# Revit family: Shower-Valves_and_Controls-KALLISTA-Rough_In-P29527
name_source: partatom
category: Plumbing Fixtures
units: mm (PartAtom-declared; Revit-internal decimal feet)

## family parameters
Cut with Voids When Loaded = No
Host = Face
Maintain Annotation Orientation = No
OmniClass Number = 23.27.31.00
OmniClass Title = Valves
Part Type = Normal
Room Calculation Point = No
Round Connector Dimension = Use Diameter
Shared = No

## types (1)
- NA-Stainless Steel
    ADA Compliant = No
    Assembly Code = D2020
    CW Connection = Yes
    Cold Water Inlet = Cold Water Inlet
    Date Modified = 06/23/2025
    Default Elevation = 36"
    Description = 1/2 Inch Volume Control Rough-In Assembly
    Finish = Kallista-Metal-NA-Stainless_Steel
    Flow Rate = 0 GPM
    HW Connection = Yes
    Height = 2 3/8"
    Hot Water Inlet = Hot Water Inlet
    Length = 3 5/16"
    Manufacturer = Kallista Co.
    Master Format 2014 = 23 09 13.33
    Master Format 2014 Name = Control Valves
    Material = Premium Metal Construction
    Model = P29527-00-NA
    Pressure = 0.00 psi
    Product Documentation Link = https://techcomm.kohler.com
    Product Name = Rough In
    Product Page URL = https://www.kallista.com
    Type = 1
    URL = https://www.kallista.com
    Vent Connection = No
    Waste Connection = No
    Waste Water Outlet = Waste Water Outlet
    WaterSense Certified = No
    Width = 1 3/4"

## geometry (parser evidence)
native form markers: Sweep x6
no freeform markers — native parametric forms only
